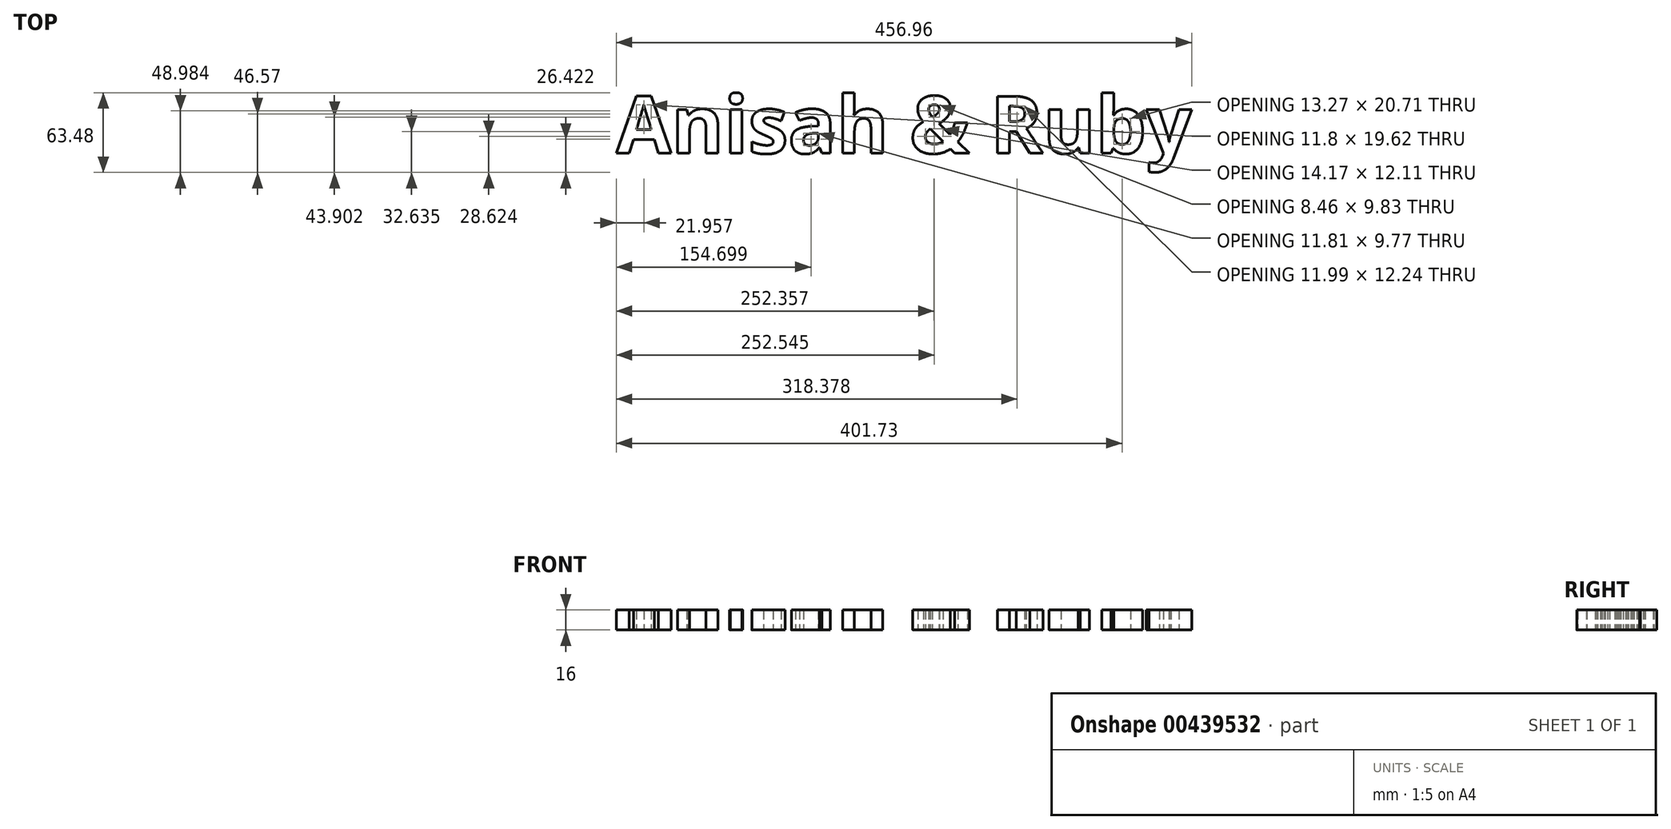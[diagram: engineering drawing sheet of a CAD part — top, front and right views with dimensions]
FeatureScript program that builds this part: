
annotation { "Feature Type Name" : "Feature", "Feature Type Description" : "" }
export const myFeature = defineFeature(function(context is Context, id is Id, definition is map)
    precondition{}
    {
        {
            var Q0;
            Q0=qCreatedBy(makeId("Top.planeOp"),FACE);
            var sketch = newSketch(context, id + "F0", { "sketchPlane" : qUnion([Q0])});
            skText(sketch, "E0", { "text": "Anisah & Ruby", "fontName": "OpenSans-Bold.ttf"});
            const initialGuessF0  = {"E0": [0, 0, 1, 0, 0.0457]};
            skSetInitialGuess(sketch, initialGuessF0);
            skSolve(sketch);
        }
        {
            var Q0;
            Q0 = qSketchRegion(id + "F0", true);
            extrude(context, id + "F1", {"entities" : qUnion([Q0]), "depth" : 16 * mm});
        }
    });
